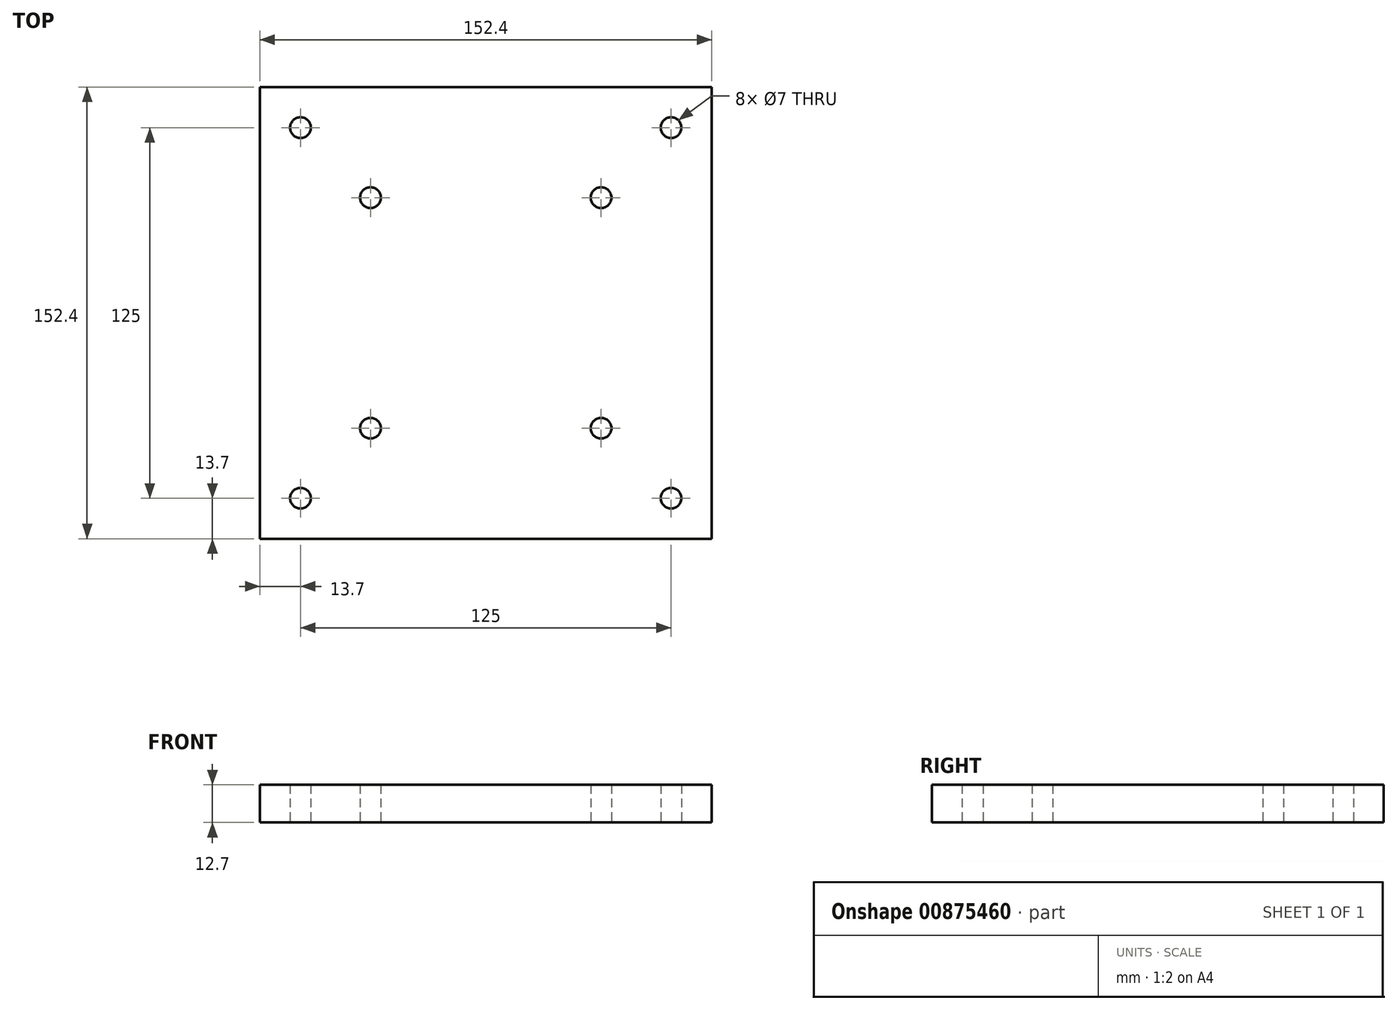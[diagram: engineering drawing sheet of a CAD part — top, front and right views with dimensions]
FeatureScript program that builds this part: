
annotation { "Feature Type Name" : "Feature", "Feature Type Description" : "" }
export const myFeature = defineFeature(function(context is Context, id is Id, definition is map)
    precondition{}
    {
        {
            var Q0;
            Q0=qCreatedBy(makeId("Top.planeOp"),FACE);
            var sketch = newSketch(context, id + "F0", { "sketchPlane" : qUnion([Q0])});
            skCircle(sketch, "E0", {"center": v(0, 0) * mm, "radius": 55 * mm, "construction": true});
            skLineSegment(sketch, "E1.bottom", {"start": v(-76.2, 76.2) * mm, "end": v(76.2, 76.2) * mm});
            skLineSegment(sketch, "E1.top", {"start": v(-76.2, -76.2) * mm, "end": v(76.2, -76.2) * mm});
            skLineSegment(sketch, "E1.left", {"start": v(-76.2, 76.2) * mm, "end": v(-76.2, -76.2) * mm});
            skLineSegment(sketch, "E1.right", {"start": v(76.2, 76.2) * mm, "end": v(76.2, -76.2) * mm});
            skLineSegment(sketch, "E2", {"start": v(-76.2, 76.2) * mm, "end": v(76.2, -76.2) * mm, "construction": true});
            skLineSegment(sketch, "E3", {"start": v(76.2, 76.2) * mm, "end": v(-76.2, -76.2) * mm, "construction": true});
            skCircle(sketch, "E4", {"center": v(-62.5, 62.5) * mm, "radius": 3.5 * mm});
            skCircle(sketch, "E5", {"center": v(62.5, 62.5) * mm, "radius": 3.5 * mm});
            skCircle(sketch, "E6", {"center": v(62.5, -62.5) * mm, "radius": 3.5 * mm});
            skCircle(sketch, "E7", {"center": v(-62.5, -62.5) * mm, "radius": 3.5 * mm});
            skCircle(sketch, "E8", {"center": v(-38.9, 38.9) * mm, "radius": 3.5 * mm});
            skCircle(sketch, "E9", {"center": v(38.9, 38.9) * mm, "radius": 3.5 * mm});
            skCircle(sketch, "E10", {"center": v(38.9, -38.9) * mm, "radius": 3.5 * mm});
            skCircle(sketch, "E11", {"center": v(-38.9, -38.9) * mm, "radius": 3.5 * mm});
            skCircle(sketch, "E12", {"center": v(0, 0) * mm, "radius": 88.39 * mm, "construction": true});
            skSolve(sketch);
        }
        {
            var Q0;
            Q0 = qSketchRegion(id + "F0", true);
            extrude(context, id + "F1", {"entities" : qUnion([Q0]), "depth" : 12.7 * mm, "offsetDistance" : 25 * mm});
        }
    });
